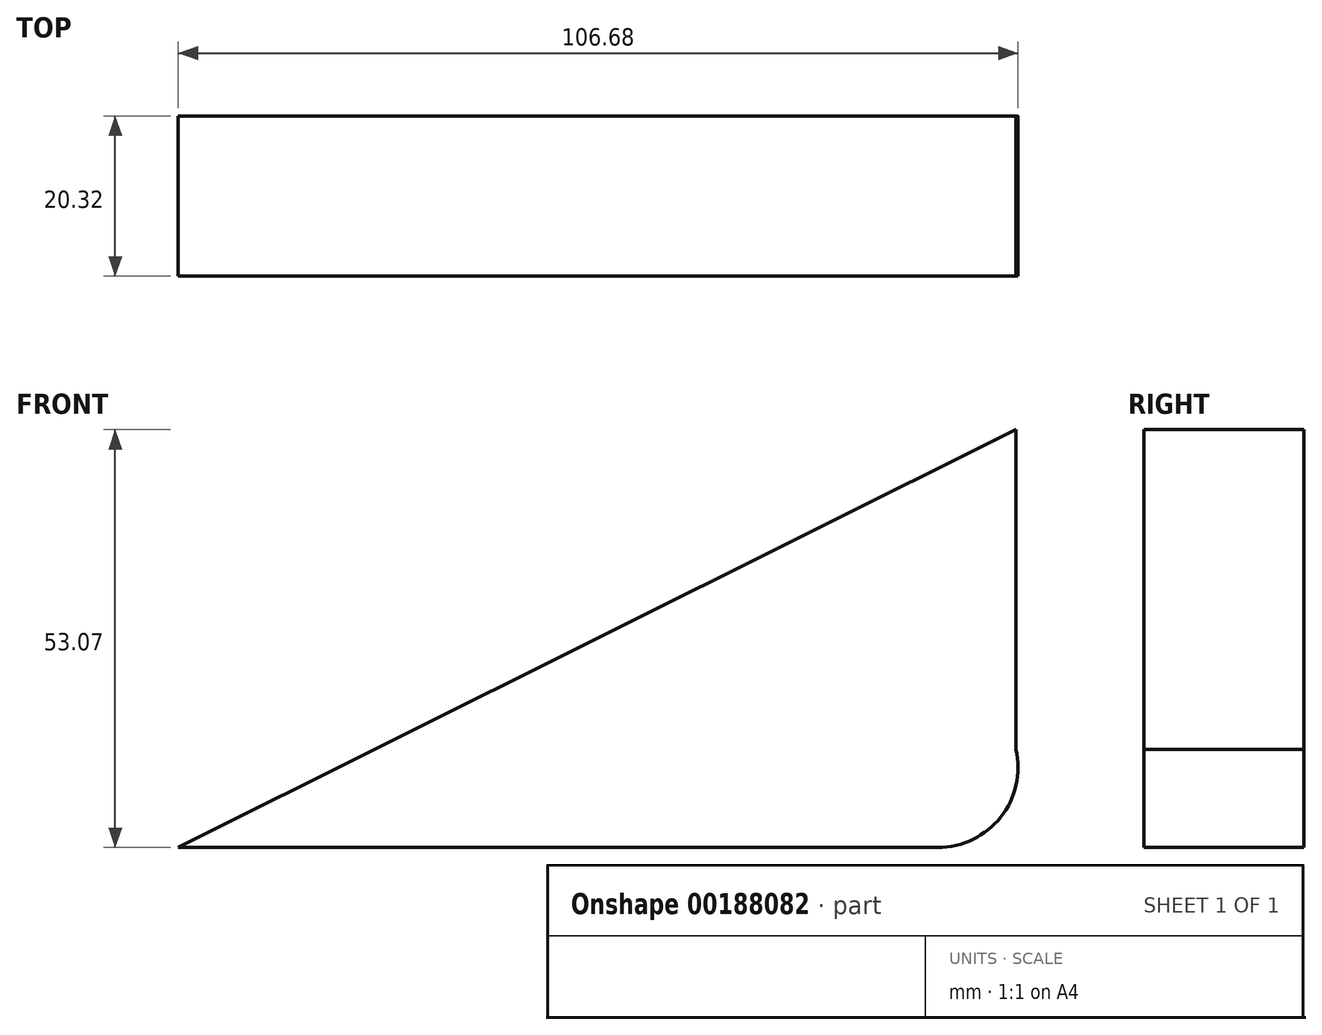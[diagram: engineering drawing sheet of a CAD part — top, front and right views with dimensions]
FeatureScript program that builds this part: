
annotation { "Feature Type Name" : "Feature", "Feature Type Description" : "" }
export const myFeature = defineFeature(function(context is Context, id is Id, definition is map)
    precondition{}
    {
        {
            var Q0;
            Q0=qCreatedBy(makeId("Front.planeOp"),FACE);
            var sketch = newSketch(context, id + "F0", { "sketchPlane" : qUnion([Q0])});
            skLineSegment(sketch, "E0", {"start": v(-48.54, 0) * mm, "end": v(47.98, 0) * mm});
            skArc(sketch, "E1", {"start": v(47.98, 0) * mm, "mid": v(55.93, 3.83) * mm, "end": v(57.89, 12.43) * mm});
            skLineSegment(sketch, "E2", {"start": v(57.89, 12.43) * mm, "end": v(57.89, 53.07) * mm});
            skLineSegment(sketch, "E3", {"start": v(57.89, 53.07) * mm, "end": v(-48.54, 0) * mm});
            skSolve(sketch);
        }
        {
            var Q0;
            Q0=makeQuery(id+"F0.imprint","IMPRINT",FACE,{"disambiguationData":[TD([[makeQuery(id+"F0.imprint","IMPRINT",EDGE,{"derivedFrom":sQuery(id+"F0.wireOp",EDGE,"E0")}),1.0]])]});
            extrude(context, id + "F1", {"entities" : qUnion([Q0]), "depth" : 20.32 * mm});
        }
    });
